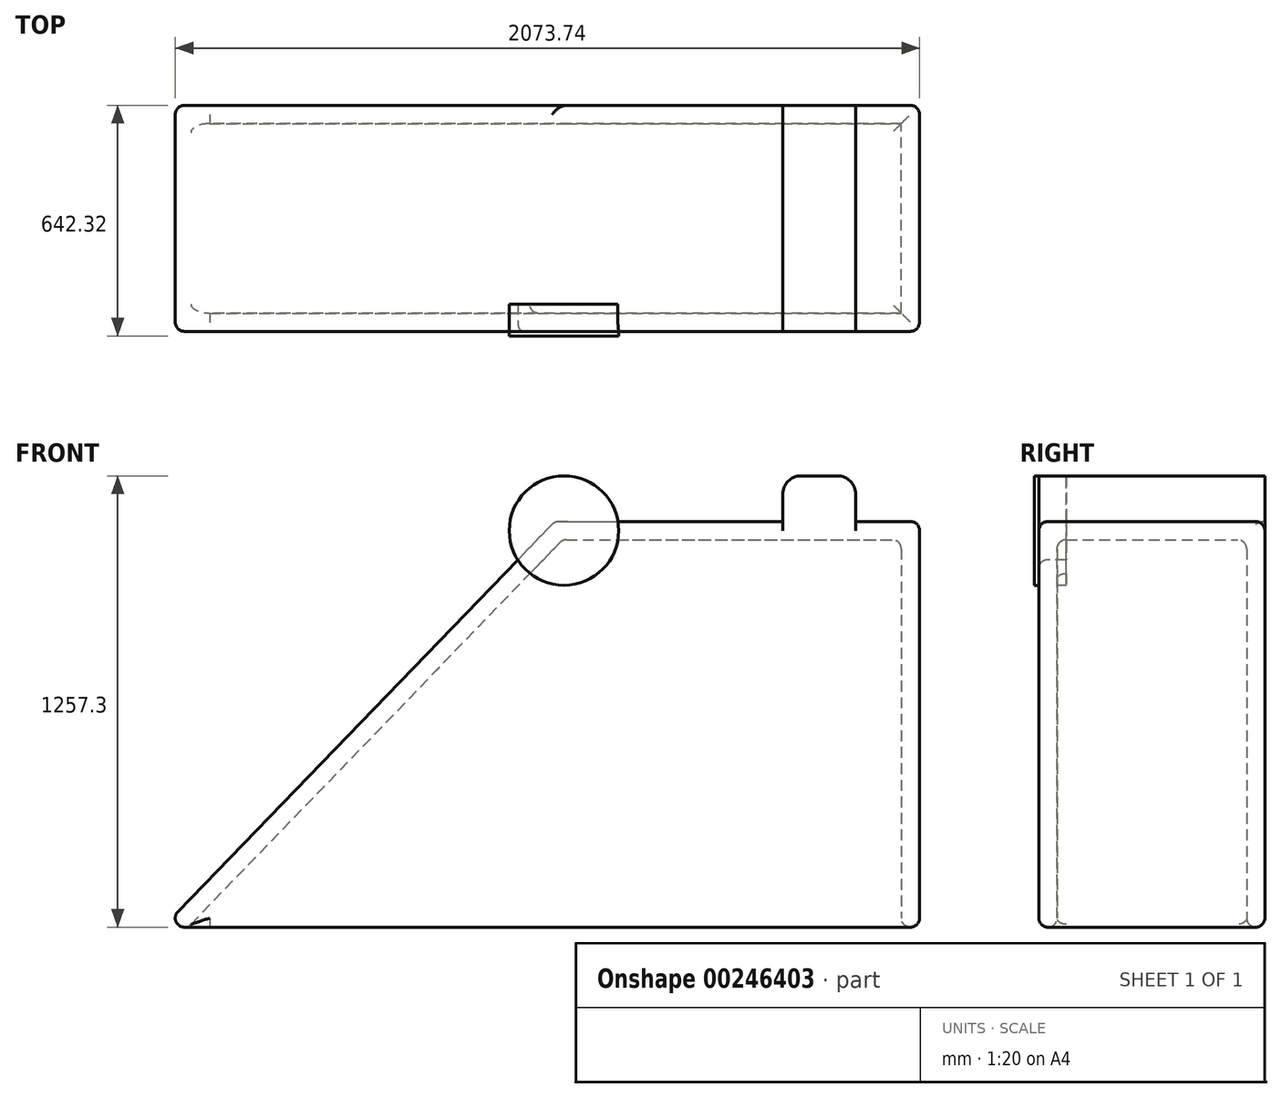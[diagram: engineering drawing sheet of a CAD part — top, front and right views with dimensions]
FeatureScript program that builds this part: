
annotation { "Feature Type Name" : "Feature", "Feature Type Description" : "" }
export const myFeature = defineFeature(function(context is Context, id is Id, definition is map)
    precondition{}
    {
        {
            var Q0;
            Q0=qCreatedBy(makeId("Front.planeOp"),FACE);
            var sketch = newSketch(context, id + "F0", { "sketchPlane" : qUnion([Q0])});
            skLineSegment(sketch, "E0.top", {"start": v(1054.1, -565.15) * mm, "end": v(-1054.1, -565.15) * mm});
            skLineSegment(sketch, "E0.left", {"start": v(1054.1, 565.15) * mm, "end": v(1054.1, -565.15) * mm});
            skPoint(sketch, "E0.middle", {"position": v(0, 0) * mm});
            skLineSegment(sketch, "E1", {"start": v(-1054.1, -565.15) * mm, "end": v(38.1, 565.15) * mm});
            skLineSegment(sketch, "E2", {"start": v(38.1, 565.15) * mm, "end": v(1054.1, 565.15) * mm});
            skSolve(sketch);
        }
        {
            var Q0;
            Q0 = qSketchRegion(id + "F0", true);
            extrude(context, id + "F1", {"entities" : qUnion([Q0]), "depth" : 49.5 / 50.8 * mm, "hasSecondDirection" : true, "secondDirectionOppositeDirection" : true, "secondDirectionDepth" : 628.65 * mm});
        }
        {
            var Q0;
            Q0=makeQuery(id+"F1.opExtrude","SWEPT_FACE",FACE,{"disambiguationData":[OSD([sQuery(id+"F0.wireOp",EDGE,"E0.top")])]});
            shell(context, id + "F2", {"entities" : qUnion([Q0]), "thickness" : 50.8 * mm});
        }
        {
            var Q0;
            Q0=makeQuery(id+"F1.opExtrude","CAP_FACE",FACE,{"disambiguationData":[OSD([sQuery(id+"F0.wireOp",EDGE,"E0.top"),sQuery(id+"F0.wireOp",EDGE,"E0.left"),sQuery(id+"F0.wireOp",EDGE,"E1"),sQuery(id+"F0.wireOp",EDGE,"E2")])],"isStart":false});
            var sketch = newSketch(context, id + "F3", { "sketchPlane" : qUnion([Q0])});
            skLineSegment(sketch, "E3", {"start": v(1054.1, 539.75) * mm, "end": v(63.5, 539.75) * mm, "construction": true});
            skLineSegment(sketch, "E4", {"start": v(63.5, 539.75) * mm, "end": v(63.5, -565.15) * mm, "construction": true});
            skCircle(sketch, "E5", {"center": v(63.5, 539.75) * mm, "radius": 152.4 * mm});
            skSolve(sketch);
        }
        {
            var Q0;
            Q0 = qSketchRegion(id + "F3", true);
            extrude(context, id + "F4", {"entities" : qUnion([Q0]), "operationType" : NewBodyOperationType.ADD, "oppositeDirection" : true, "depth" : 76.2 * mm, "hasSecondDirection" : true, "secondDirectionOppositeDirection" : false, "secondDirectionDepth" : 12.7 * mm});
        }
        {
            var Q0;
            Q0=makeQuery(id+"F1.opExtrude","CAP_FACE",FACE,{"disambiguationData":[OSD([sQuery(id+"F0.wireOp",EDGE,"E0.top"),sQuery(id+"F0.wireOp",EDGE,"E0.left"),sQuery(id+"F0.wireOp",EDGE,"E1"),sQuery(id+"F0.wireOp",EDGE,"E2")])],"isStart":false});
            var sketch = newSketch(context, id + "F5", { "sketchPlane" : qUnion([Q0])});
            skLineSegment(sketch, "E6.bottom", {"start": v(876.3, 565.15) * mm, "end": v(673.1, 565.15) * mm});
            skLineSegment(sketch, "E6.top", {"start": v(876.3, 692.15) * mm, "end": v(673.1, 692.15) * mm});
            skLineSegment(sketch, "E6.left", {"start": v(876.3, 565.15) * mm, "end": v(876.3, 692.15) * mm});
            skLineSegment(sketch, "E6.right", {"start": v(673.1, 565.15) * mm, "end": v(673.1, 692.15) * mm});
            skLineSegment(sketch, "E7", {"start": v(774.7, 692.15) * mm, "end": v(774.7, -565.15) * mm, "construction": true});
            skLineSegment(sketch, "E8", {"start": v(876.3, 692.15) * mm, "end": v(1054.1, 692.15) * mm, "construction": true});
            skSolve(sketch);
        }
        {
            var Q0;
            Q0 = qSketchRegion(id + "F5", true);
            var Q1;
            Q1=makeQuery(id+"F1.opExtrude","CAP_FACE",FACE,{"disambiguationData":[OSD([sQuery(id+"F0.wireOp",EDGE,"E0.top"),sQuery(id+"F0.wireOp",EDGE,"E0.left"),sQuery(id+"F0.wireOp",EDGE,"E1"),sQuery(id+"F0.wireOp",EDGE,"E2")])],"isStart":true});
            extrude(context, id + "F6", {"entities" : qUnion([Q0]), "operationType" : NewBodyOperationType.ADD, "endBound" : BoundingType.UP_TO_SURFACE, "oppositeDirection" : true, "endBoundEntityFace" : qUnion([Q1]), "depth" : 25.4 * mm});
        }
        {
            var Q0;
            Q0=makeQuery(id+"F1.opExtrude","CAP_EDGE",EDGE,{"disambiguationData":[OSD([sQuery(id+"F0.wireOp",EDGE,"E0.left")])],"isStart":false});
            var Q1;
            Q1=makeQuery(id+"F1.opExtrude","CAP_EDGE",EDGE,{"disambiguationData":[OSD([sQuery(id+"F0.wireOp",EDGE,"E0.left")])],"isStart":true});
            var Q2;
            Q2=makeQuery(id+"F1.opExtrude","SWEPT_EDGE",EDGE,{"disambiguationData":[OSD([sQuery(id+"F0.wireOp",EDGE,"E0.left"),sQuery(id+"F0.wireOp",EDGE,"E2")])]});
            var Q3;
            Q3=makeQuery(id+"F1.opExtrude","SWEPT_EDGE",EDGE,{"disambiguationData":[OSD([sQuery(id+"F0.wireOp",EDGE,"E0.top"),sQuery(id+"F0.wireOp",EDGE,"E0.left")])]});
            var Q4;
            Q4=makeQuery(id+"F1.opExtrude","CAP_EDGE",EDGE,{"disambiguationData":[OSD([sQuery(id+"F0.wireOp",EDGE,"E0.top")])],"isStart":true});
            var Q5;
            {var subQ0=sQuery(id+"F0.wireOp",EDGE,"E0.top");Q5=makeQuery(id+"F2.opShell","OFFSET_EDGE",EDGE,{"disambiguationData":[OSD([subQ0]),TDD([makeQuery(id+"F1.opExtrude","CAP_EDGE",EDGE,{"disambiguationData":[OSD([subQ0])],"isStart":true})])]});}
            var Q6;
            Q6=makeQuery(id+"F2.opShell","OFFSET_EDGE",EDGE,{"disambiguationData":[OSD([sQuery(id+"F0.wireOp",EDGE,"E0.top"),sQuery(id+"F0.wireOp",EDGE,"E0.left")])]});
            var Q7;
            {var subQ0=sQuery(id+"F0.wireOp",EDGE,"E0.top");Q7=makeQuery(id+"F2.opShell","OFFSET_EDGE",EDGE,{"disambiguationData":[OSD([subQ0]),TDD([makeQuery(id+"F1.opExtrude","CAP_EDGE",EDGE,{"disambiguationData":[OSD([subQ0])],"isStart":false})])]});}
            var Q8;
            Q8=makeQuery(id+"F1.opExtrude","CAP_EDGE",EDGE,{"disambiguationData":[OSD([sQuery(id+"F0.wireOp",EDGE,"E0.top")])],"isStart":false});
            var Q9;
            Q9=makeQuery(id+"F2.opShell","OFFSET_EDGE",EDGE,{"disambiguationData":[OSD([sQuery(id+"F0.wireOp",EDGE,"E0.top"),sQuery(id+"F0.wireOp",EDGE,"E1")])]});
            var Q10;
            Q10=makeQuery(id+"F1.opExtrude","SWEPT_EDGE",EDGE,{"disambiguationData":[OSD([sQuery(id+"F0.wireOp",EDGE,"E0.top"),sQuery(id+"F0.wireOp",EDGE,"E1")])]});
            var Q11;
            {var subQ0=sQuery(id+"F0.wireOp",EDGE,"E1");Q11=makeQuery(id+"F2.opShell","OFFSET_EDGE",EDGE,{"disambiguationData":[OSD([subQ0]),TDD([makeQuery(id+"F1.opExtrude","CAP_EDGE",EDGE,{"disambiguationData":[OSD([subQ0])],"isStart":true})])]});}
            var Q12;
            {var subQ0=sQuery(id+"F0.wireOp",EDGE,"E1");Q12=makeQuery(id+"F2.opShell","OFFSET_EDGE",EDGE,{"disambiguationData":[OSD([subQ0]),TDD([makeQuery(id+"F1.opExtrude","CAP_EDGE",EDGE,{"disambiguationData":[OSD([subQ0])],"isStart":false})])]});}
            var Q13;
            Q13=makeQuery(id+"F2.opShell","OFFSET_EDGE",EDGE,{"disambiguationData":[OSD([sQuery(id+"F0.wireOp",EDGE,"E1"),sQuery(id+"F0.wireOp",EDGE,"E2")])]});
            var Q14;
            {var subQ0=sQuery(id+"F0.wireOp",EDGE,"E2");Q14=makeQuery(id+"F2.opShell","OFFSET_EDGE",EDGE,{"disambiguationData":[OSD([subQ0]),TDD([makeQuery(id+"F1.opExtrude","CAP_EDGE",EDGE,{"disambiguationData":[OSD([subQ0])],"isStart":false})])]});}
            var Q15;
            {var subQ0=sQuery(id+"F0.wireOp",EDGE,"E2");Q15=makeQuery(id+"F2.opShell","OFFSET_EDGE",EDGE,{"disambiguationData":[OSD([subQ0]),TDD([makeQuery(id+"F1.opExtrude","CAP_EDGE",EDGE,{"disambiguationData":[OSD([subQ0])],"isStart":true})])]});}
            var Q16;
            Q16=makeQuery(id+"F2.opShell","OFFSET_EDGE",EDGE,{"disambiguationData":[OSD([sQuery(id+"F0.wireOp",EDGE,"E0.left"),sQuery(id+"F0.wireOp",EDGE,"E2")])]});
            var Q17;
            Q17=makeQuery(id+"F1.opExtrude","CAP_EDGE",EDGE,{"disambiguationData":[OSD([sQuery(id+"F0.wireOp",EDGE,"E1")])],"isStart":false});
            var Q18;
            Q18=makeQuery(id+"F1.opExtrude","CAP_EDGE",EDGE,{"disambiguationData":[OSD([sQuery(id+"F0.wireOp",EDGE,"E1")])],"isStart":true});
            var Q19;
            Q19=makeQuery(id+"F1.opExtrude","SWEPT_EDGE",EDGE,{"disambiguationData":[OSD([sQuery(id+"F0.wireOp",EDGE,"E1"),sQuery(id+"F0.wireOp",EDGE,"E2")])]});
            var Q20;
            {var subQ0=sQuery(id+"F0.wireOp",EDGE,"E2");Q20=makeQuery(id+"F6.boolean.opBoolean","SPLIT",EDGE,{"disambiguationData":[TD([makeQuery(id+"F4.opExtrude","SWEPT_FACE",FACE,{"disambiguationData":[OSD([sQuery(id+"F3.wireOp",EDGE,"E5")])]})])],"derivedFrom":makeQuery(id+"F1.opExtrude","CAP_EDGE",EDGE,{"disambiguationData":[OSD([subQ0])],"isStart":false})});}
            var Q21;
            {var subQ0=sQuery(id+"F0.wireOp",EDGE,"E2");var subQ2=sQuery(id+"F0.wireOp",EDGE,"E0.left");Q21=makeQuery(id+"F6.boolean.opBoolean","SPLIT",EDGE,{"disambiguationData":[TD([makeQuery(id+"F1.opExtrude","SWEPT_FACE",FACE,{"disambiguationData":[OSD([subQ2])]})])],"derivedFrom":makeQuery(id+"F1.opExtrude","CAP_EDGE",EDGE,{"disambiguationData":[OSD([subQ0])],"isStart":false})});}
            var Q22;
            {var subQ0=sQuery(id+"F0.wireOp",EDGE,"E2");Q22=makeQuery(id+"F6.boolean.opBoolean","SPLIT",EDGE,{"disambiguationData":[TD([makeQuery(id+"FCoeUZboU5xHGXm_1.1.F4.opExtrude","SWEPT_FACE",FACE,{"disambiguationData":[OSD([sQuery(id+"F3.wireOp",EDGE,"E5")])]})])],"derivedFrom":makeQuery(id+"F1.opExtrude","CAP_EDGE",EDGE,{"disambiguationData":[OSD([subQ0])],"isStart":true})});}
            var Q23;
            {var subQ0=sQuery(id+"F0.wireOp",EDGE,"E2");var subQ2=sQuery(id+"F0.wireOp",EDGE,"E0.left");Q23=makeQuery(id+"F6.boolean.opBoolean","SPLIT",EDGE,{"disambiguationData":[TD([makeQuery(id+"F1.opExtrude","SWEPT_FACE",FACE,{"disambiguationData":[OSD([subQ2])]})])],"derivedFrom":makeQuery(id+"F1.opExtrude","CAP_EDGE",EDGE,{"disambiguationData":[OSD([subQ0])],"isStart":true})});}
            fillet(context, id + "F7", {"entities" : qUnion([Q0, Q1, Q2, Q3, Q4, Q5, Q6, Q7, Q8, Q9, Q10, Q11, Q12, Q13, Q14, Q15, Q16, Q17, Q18, Q19, Q20, Q21, Q22, Q23]), "radius" : 25.4 * mm, "tangentPropagation" : true, "allowEdgeOverflow" : false});
        }
        {
            var Q0;
            Q0=makeQuery(id+"F6.opExtrude","SWEPT_EDGE",EDGE,{"disambiguationData":[OSD([sQuery(id+"F5.wireOp",EDGE,"E6.top"),sQuery(id+"F5.wireOp",EDGE,"E6.left")])]});
            var Q1;
            Q1=makeQuery(id+"F6.opExtrude","SWEPT_EDGE",EDGE,{"disambiguationData":[OSD([sQuery(id+"F5.wireOp",EDGE,"E6.top"),sQuery(id+"F5.wireOp",EDGE,"E6.right")])]});
            fillet(context, id + "F8", {"entities" : qUnion([Q0, Q1]), "radius" : 50.8 * mm, "tangentPropagation" : true, "allowEdgeOverflow" : false});
        }
    });
